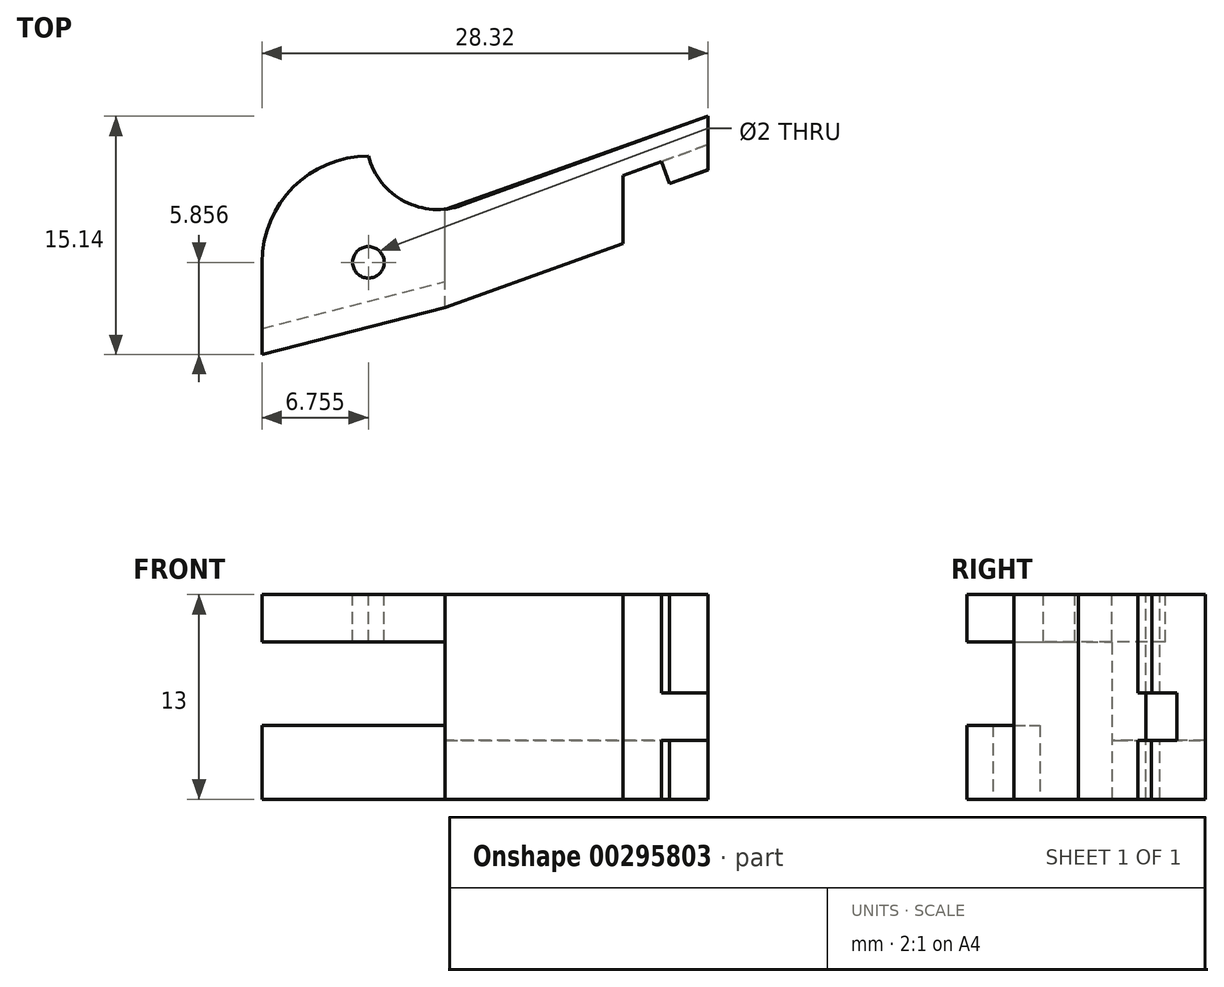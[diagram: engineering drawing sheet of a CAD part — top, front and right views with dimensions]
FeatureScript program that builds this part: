
annotation { "Feature Type Name" : "Feature", "Feature Type Description" : "" }
export const myFeature = defineFeature(function(context is Context, id is Id, definition is map)
    precondition{}
    {
        {
            var Q0;
            Q0=qCreatedBy(makeId("Right.planeOp"),FACE);
            var sketch = newSketch(context, id + "F0", { "sketchPlane" : qUnion([Q0])});
            skLineSegment(sketch, "E0.bottom", {"start": v(-1.75, 5.5) * mm, "end": v(0, 5.5) * mm});
            skLineSegment(sketch, "E0.top", {"start": v(-1.75, 8.5) * mm, "end": v(0, 8.5) * mm});
            skLineSegment(sketch, "E0.left", {"start": v(-1.75, 8.5) * mm, "end": v(-1.75, 5.5) * mm});
            skLineSegment(sketch, "E0.right", {"start": v(0, 8.5) * mm, "end": v(0, 5.5) * mm});
            skLineSegment(sketch, "E1.bottom", {"start": v(-3.4, 8.5) * mm, "end": v(-1.75, 8.5) * mm});
            skLineSegment(sketch, "E1.top", {"start": v(-3.4, -8.5) * mm, "end": v(-1.75, -8.5) * mm});
            skLineSegment(sketch, "E1.left", {"start": v(-1.75, 8.5) * mm, "end": v(-1.75, -8.5) * mm});
            skLineSegment(sketch, "E1.right", {"start": v(-3.4, 8.5) * mm, "end": v(-3.4, -8.5) * mm});
            skLineSegment(sketch, "E2.bottom", {"start": v(-1.75, -8.5) * mm, "end": v(0, -8.5) * mm});
            skLineSegment(sketch, "E2.top", {"start": v(-1.75, -5.5) * mm, "end": v(0, -5.5) * mm});
            skLineSegment(sketch, "E2.left", {"start": v(-1.75, -5.5) * mm, "end": v(-1.75, -8.5) * mm});
            skLineSegment(sketch, "E2.right", {"start": v(0, -5.5) * mm, "end": v(0, -8.5) * mm});
            skPoint(sketch, "E3", {"position": v(-1.75, 0) * mm});
            skLineSegment(sketch, "E4", {"start": v(-1.75, 5.5) * mm, "end": v(-1.75, -5.5) * mm});
            skLineSegment(sketch, "E5", {"start": v(-3.4, 8.5) * mm, "end": v(0, 8.5) * mm});
            skLineSegment(sketch, "E6", {"start": v(-1.75, -5.5) * mm, "end": v(-3.4, -5.5) * mm});
            skLineSegment(sketch, "E7", {"start": v(0, 5.5) * mm, "end": v(0, 8.5) * mm});
            skLineSegment(sketch, "E8", {"start": v(0, -8.5) * mm, "end": v(0, -8.5) * mm});
            skSolve(sketch);
        }
        {
            var Q0;
            Q0=qCreatedBy(makeId("Top.planeOp"),FACE);
            var Q1;
            Q1=sQuery(id+"F0.wireOp",VERTEX,"E1.left.start");
            cPlane(context, id + "F1", {"entities" : qUnion([Q0, Q1]), "cplaneType" : CPlaneType.PLANE_POINT, "offset" : 25 * mm, "width" : 150 * mm, "height" : 150 * mm});
        }
        {
            var Q0;
            Q0=qCreatedBy(id+"F1.planeOp",FACE);
            var sketch = newSketch(context, id + "F2", { "sketchPlane" : qUnion([Q0])});
            skLineSegment(sketch, "E9", {"start": v(0, 0) * mm, "end": v(-15.6, -5.66) * mm});
            skLineSegment(sketch, "E10", {"start": v(-5.4, -8.07) * mm, "end": v(-5.4, -3.77) * mm});
            skLineSegment(sketch, "E11", {"start": v(-5.4, -3.77) * mm, "end": v(-2.95, -2.88) * mm});
            skLineSegment(sketch, "E12", {"start": v(-2.95, -2.88) * mm, "end": v(-2.44, -4.29) * mm});
            skLineSegment(sketch, "E13", {"start": v(-2.44, -4.29) * mm, "end": v(0, -3.4) * mm});
            skLineSegment(sketch, "E14", {"start": v(-28.3, -15.14) * mm, "end": v(-28.3, -9.28) * mm});
            skCircle(sketch, "E15", {"center": v(-21.56, -9.28) * mm, "radius": 1 * mm});
            skArc(sketch, "E16", {"start": v(-21.56, -2.53) * mm, "mid": v(-26.33, -4.51) * mm, "end": v(-28.3, -9.28) * mm});
            skCircle(sketch, "E17", {"center": v(-21.56, -9.28) * mm, "radius": 4.5 * mm, "construction": true});
            skArc(sketch, "E18", {"start": v(-21.56, -2.53) * mm, "mid": v(-19.26, -5.4) * mm, "end": v(-15.6, -5.66) * mm});
            skLineSegment(sketch, "E19", {"start": v(-18.64, -6.76) * mm, "end": v(-16.68, -12.17) * mm, "construction": true});
            skLineSegment(sketch, "E20", {"start": v(0, 0) * mm, "end": v(0, -3.4) * mm});
            skLineSegment(sketch, "E21", {"start": v(-19.37, -5.35) * mm, "end": v(-21.07, -8.41) * mm, "construction": true});
            skLineSegment(sketch, "E22", {"start": v(-2.95, -2.88) * mm, "end": v(0, -1.8) * mm});
            skLineSegment(sketch, "E23", {"start": v(-5.4, -8.07) * mm, "end": v(-7.36, -2.67) * mm, "construction": true});
            skLineSegment(sketch, "E24", {"start": v(-5.4, -3.77) * mm, "end": v(-5.4, -8.07) * mm});
            skLineSegment(sketch, "E25", {"start": v(-28.3, -15.14) * mm, "end": v(-16.68, -12.17) * mm});
            skLineSegment(sketch, "E26", {"start": v(-16.68, -12.17) * mm, "end": v(-5.4, -8.07) * mm});
            skPoint(sketch, "E27", {"position": v(-21.3, -10.25) * mm});
            skLineSegment(sketch, "E28", {"start": v(-21.3, -10.25) * mm, "end": v(-20.56, -13.16) * mm, "construction": true});
            skLineSegment(sketch, "E29", {"start": v(-21.56, -2.53) * mm, "end": v(-21.56, -8.28) * mm, "construction": true});
            skLineSegment(sketch, "E30", {"start": v(-15.6, -5.66) * mm, "end": v(-18.64, -6.76) * mm, "construction": true});
            skLineSegment(sketch, "E31", {"start": v(-16.68, -12.17) * mm, "end": v(-16.68, -5.9) * mm});
            skSolve(sketch);
        }
        {
            var Q0;
            Q0=makeQuery(id+"F2.imprint","IMPRINT",FACE,{"disambiguationData":[TD([[makeQuery(id+"F2.imprint","IMPRINT",EDGE,{"derivedFrom":sQuery(id+"F2.wireOp",EDGE,"E14")}),-1.0]])]});
            var Q1;
            Q1=sQuery(id+"F0.wireOp",VERTEX,"E0.right.start");
            extrude(context, id + "F3", {"entities" : qUnion([Q0]), "oppositeDirection" : true, "endBoundEntityVertex" : qUnion([Q1]), "depth" : 3 * mm});
        }
        {
            var Q0;
            {var subQ2=sQuery(id+"F2.wireOp",EDGE,"E9");Q0=makeQuery(id+"F2.imprint","IMPRINT",FACE,{"disambiguationData":[TD([[makeQuery(id+"F2.imprint","IMPRINT",EDGE,{"derivedFrom":subQ2}),1.0]])]});}
            var Q1;
            Q1=sQuery(id+"F0.wireOp",VERTEX,"E2.left.start");
            extrude(context, id + "F4", {"entities" : qUnion([Q0]), "operationType" : NewBodyOperationType.ADD, "oppositeDirection" : true, "endBoundEntityVertex" : qUnion([Q1]), "depth" : 13 * mm});
        }
        {
            var Q0;
            Q0=makeQuery(id+"F2.imprint","IMPRINT",FACE,{"disambiguationData":[TD([[makeQuery(id+"F2.imprint","IMPRINT",EDGE,{"derivedFrom":sQuery(id+"F2.wireOp",EDGE,"E12")}),1.0]])]});
            extrude(context, id + "F5", {"entities" : qUnion([Q0]), "operationType" : NewBodyOperationType.ADD, "oppositeDirection" : true, "depth" : (3.75 + 2.5) * mm});
        }
        {
            var Q0;
            Q0=qCreatedBy(id+"F1.planeOp",FACE);
            cPlane(context, id + "F6", {"entities" : qUnion([Q0]), "cplaneType" : CPlaneType.OFFSET, "offset" : 13 * mm, "oppositeDirection" : true, "width" : 150 * mm, "height" : 150 * mm});
        }
        {
            var Q0;
            Q0=qCreatedBy(id+"F6.planeOp",FACE);
            var sketch = newSketch(context, id + "F7", { "sketchPlane" : qUnion([Q0])});
            skLineSegment(sketch, "E32", {"start": v(0, 0) * mm, "end": v(-16.96, -6.02) * mm});
            skLineSegment(sketch, "E33", {"start": v(-5.42, -8.02) * mm, "end": v(-5.4, -3.72) * mm});
            skLineSegment(sketch, "E34", {"start": v(-5.4, -3.72) * mm, "end": v(-2.95, -2.85) * mm});
            skLineSegment(sketch, "E35", {"start": v(-2.95, -2.85) * mm, "end": v(-2.44, -4.29) * mm});
            skLineSegment(sketch, "E36", {"start": v(-2.44, -4.29) * mm, "end": v(0, -3.42) * mm});
            skLineSegment(sketch, "E37", {"start": v(-28.3, -15.14) * mm, "end": v(-28.29, -9.26) * mm});
            skCircle(sketch, "E38", {"center": v(-21.54, -9.28) * mm, "radius": 1 * mm});
            skArc(sketch, "E39", {"start": v(-22.91, -2.67) * mm, "mid": v(-26.77, -5.01) * mm, "end": v(-28.29, -9.26) * mm});
            skCircle(sketch, "E40", {"center": v(-21.54, -9.28) * mm, "radius": 3.6 * mm, "construction": true});
            skArc(sketch, "E41", {"start": v(-22.91, -2.67) * mm, "mid": v(-20.7, -5.7) * mm, "end": v(-16.96, -6.02) * mm});
            skLineSegment(sketch, "E42", {"start": v(-18.6, -6.75) * mm, "end": v(-16.68, -12.17) * mm, "construction": true});
            skLineSegment(sketch, "E43", {"start": v(0, 0) * mm, "end": v(0, -3.42) * mm});
            skLineSegment(sketch, "E44", {"start": v(-20.18, -5.94) * mm, "end": v(-21.16, -8.35) * mm, "construction": true});
            skLineSegment(sketch, "E45", {"start": v(-2.95, -2.85) * mm, "end": v(-2.18, -2.58) * mm});
            skLineSegment(sketch, "E46", {"start": v(-5.42, -8.02) * mm, "end": v(-7.34, -2.6) * mm, "construction": true});
            skLineSegment(sketch, "E47", {"start": v(-5.4, -3.72) * mm, "end": v(-5.42, -8.02) * mm});
            skLineSegment(sketch, "E48", {"start": v(-28.3, -15.14) * mm, "end": v(-16.68, -12.17) * mm});
            skLineSegment(sketch, "E49", {"start": v(-16.68, -12.17) * mm, "end": v(-5.42, -8.02) * mm});
            skPoint(sketch, "E50", {"position": v(-21.29, -10.25) * mm});
            skLineSegment(sketch, "E51", {"start": v(-21.29, -10.25) * mm, "end": v(-20.54, -13.15) * mm, "construction": true});
            skLineSegment(sketch, "E52", {"start": v(-22.91, -2.67) * mm, "end": v(-21.74, -8.3) * mm, "construction": true});
            skLineSegment(sketch, "E53", {"start": v(-16.68, -12.17) * mm, "end": v(-16.68, -5.9) * mm});
            skLineSegment(sketch, "E54", {"start": v(-28.3, -15.14) * mm, "end": v(-28.3, -13.49) * mm});
            skLineSegment(sketch, "E55", {"start": v(-16.68, -10.5) * mm, "end": v(-16.68, -12.17) * mm});
            skLineSegment(sketch, "E56", {"start": v(-28.3, -13.49) * mm, "end": v(-16.68, -10.51) * mm});
            skSolve(sketch);
        }
        {
            var Q0;
            Q0=makeQuery(id+"F7.imprint","IMPRINT",FACE,{"disambiguationData":[TD([[makeQuery(id+"F7.imprint","IMPRINT",EDGE,{"derivedFrom":sQuery(id+"F7.wireOp",EDGE,"E37")}),-1.0]])]});
            extrude(context, id + "F8", {"entities" : qUnion([Q0]), "operationType" : NewBodyOperationType.ADD, "depth" : (2 + 1.7) * mm});
        }
        {
            var Q0;
            Q0=makeQuery(id+"F7.imprint","IMPRINT",FACE,{"disambiguationData":[TD([[makeQuery(id+"F7.imprint","IMPRINT",EDGE,{"derivedFrom":sQuery(id+"F7.wireOp",EDGE,"E48")}),1.0]])]});
            extrude(context, id + "F9", {"entities" : qUnion([Q0]), "operationType" : NewBodyOperationType.ADD, "depth" : (3 + 1.7) * mm});
        }
        {
            var Q0;
            Q0=makeQuery(id+"F7.imprint","IMPRINT",FACE,{"disambiguationData":[TD([[makeQuery(id+"F7.imprint","IMPRINT",EDGE,{"derivedFrom":sQuery(id+"F7.wireOp",EDGE,"E34")}),1.0]])]});
            extrude(context, id + "F10", {"entities" : qUnion([Q0]), "operationType" : NewBodyOperationType.ADD, "depth" : 3.75 * mm});
        }
    });
